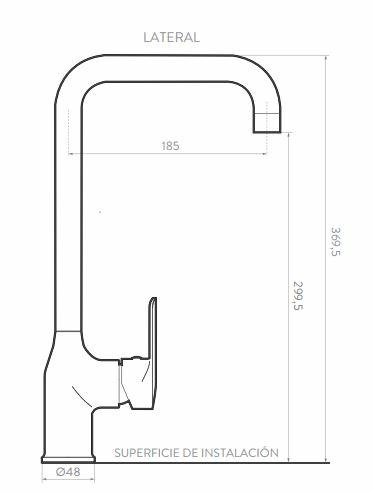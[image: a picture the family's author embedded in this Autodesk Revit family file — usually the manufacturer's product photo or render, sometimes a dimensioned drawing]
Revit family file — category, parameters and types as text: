
# Revit family: KR5035551_Grifería para Lavaplatos Monocontrol Koral Niquel
name_source: partatom
category: Plumbing Fixtures
units: mm (PartAtom-declared; Revit-internal decimal feet)

## family parameters
Cut with Voids When Loaded = No
Host = Face
OmniClass Number = 23.31.11.00
OmniClass Title = Faucets
Part Type = Normal
Room Calculation Point = No
Round Connector Dimension = Use Diameter
Shared = No

## types (1)
- KR5035551_Grifería para Lavaplatos Monocontrol Koral Niquel
    Alto = 370 mm
    Ancho = 48 mm  [stored 0.15748 ft]
    Capacidad de flujo = 60 psi: 7,28 L/min
    Creado por = IDD
    Default Elevation = 1219 mm
    Dimensiones generales producto (H * W * D) = 988 gr. - 2,17 lb
    Fabricante = Corona
    Fecha de creación = 09/10/2020
    Garantía = 30 años
    Material = Corona_Niquel
    Peso Neto aprox = 988 gr. - 2,17 lb
    Presion maxima = 125 psi (862 Kpa)
    Presion minima = 20 psi (138 Kpa)
    Profundidad = 221 mm
    Temperatura de uso = 4ºC a 60ºC
    URL = https://corona.co

note: [stored X ft] marks values corroborated as IEEE doubles in the binary element streams (Revit-internal decimal feet)

## geometry (parser evidence)
native form markers: Sweep x3
no freeform markers — native parametric forms only
